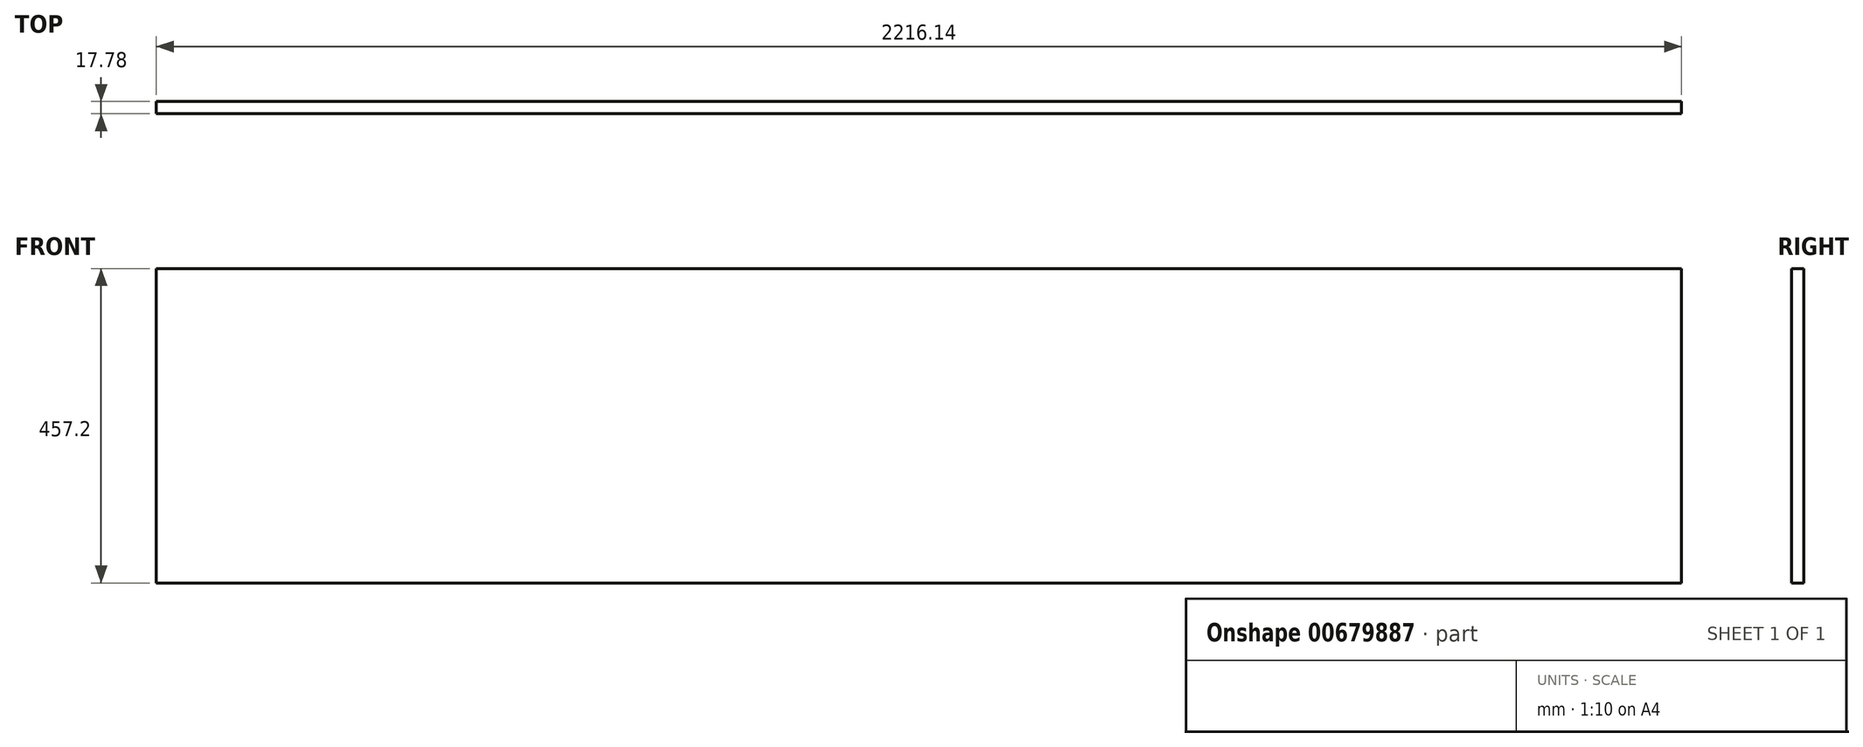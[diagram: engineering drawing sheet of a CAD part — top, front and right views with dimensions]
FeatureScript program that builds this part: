
annotation { "Feature Type Name" : "Feature", "Feature Type Description" : "" }
export const myFeature = defineFeature(function(context is Context, id is Id, definition is map)
    precondition{}
    {
        {
            var Q0;
            Q0=qCreatedBy(makeId("Front.planeOp"),FACE);
            var sketch = newSketch(context, id + "F0", { "sketchPlane" : qUnion([Q0])});
            skLineSegment(sketch, "E0.bottom", {"start": v(1108.07, 228.6) * mm, "end": v(-1108.07, 228.6) * mm});
            skLineSegment(sketch, "E0.top", {"start": v(1108.08, -228.6) * mm, "end": v(-1108.07, -228.6) * mm});
            skLineSegment(sketch, "E0.left", {"start": v(1108.07, 228.6) * mm, "end": v(1108.08, -228.6) * mm});
            skLineSegment(sketch, "E0.right", {"start": v(-1108.07, 228.6) * mm, "end": v(-1108.07, -228.6) * mm});
            skPoint(sketch, "E0.middle", {"position": v(0, 0) * mm});
            skSolve(sketch);
        }
        {
            var Q0;
            Q0=makeQuery(id+"F0.imprint","IMPRINT",FACE,{"disambiguationData":[TD([[makeQuery(id+"F0.imprint","IMPRINT",EDGE,{"derivedFrom":sQuery(id+"F0.wireOp",EDGE,"E0.bottom")}),1.0]])]});
            extrude(context, id + "F1", {"entities" : qUnion([Q0]), "endBound" : BoundingType.SYMMETRIC, "depth" : 17.78 * mm, "offsetDistance" : 25.4 * mm});
        }
    });
